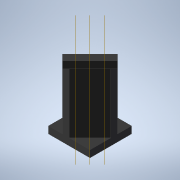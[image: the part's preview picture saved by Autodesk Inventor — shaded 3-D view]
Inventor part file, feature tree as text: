
AUTODESK INVENTOR PART (.ipt)
format: ipt  version: 2022 (Build 260153000, 153)  size: 139,776 bytes
history: native  units: in
note: dims shown in document units (in); Inventor stores cm internally (conversion verified against a paired STEP export)
features: extrude x5, sketch x5, plane x3
ambient origin geometry x8: Origin, YZ Plane, XZ Plane, XY Plane, X Axis, Y Axis, Z Axis, Center Point
bodies: Solid1 (feature_tree)
feature tree (13):
  extrude  "Extrusion1"  Depth=1.1811in
  extrude  "Extrusion2"  Depth=0.1969in TaperAngle=0.0deg
  plane  "Work Plane1"
  plane  "Work Plane2"
  plane  "Work Plane3"
  sketch  "Sketch3"  dims[d5=1.9685in d6=0.0in d7=0.2953in d8=-0.2953in]
  sketch  "Sketch4"  dims[d15=0.0787in d16=0.0in d17=0.0787in d18=0.0in]
  extrude  "Extrusion3"  Depth=1.9685in
  extrude  "Extrusion4"  Depth=0.0787in TaperAngle=0.0deg
  extrude  "Extrusion5"  Depth=0.2362in TaperAngle=0.0deg
  sketch  "Sketch1"  dims[d0=1.1811in d1=1.1811in]
  sketch  "Sketch2"  dims[d2=0.1575in d3=0.1969in d4=0.0in]
  sketch  "Sketch5"  dims[d19=0.1969in d20=0.2362in d21=0.0in]
